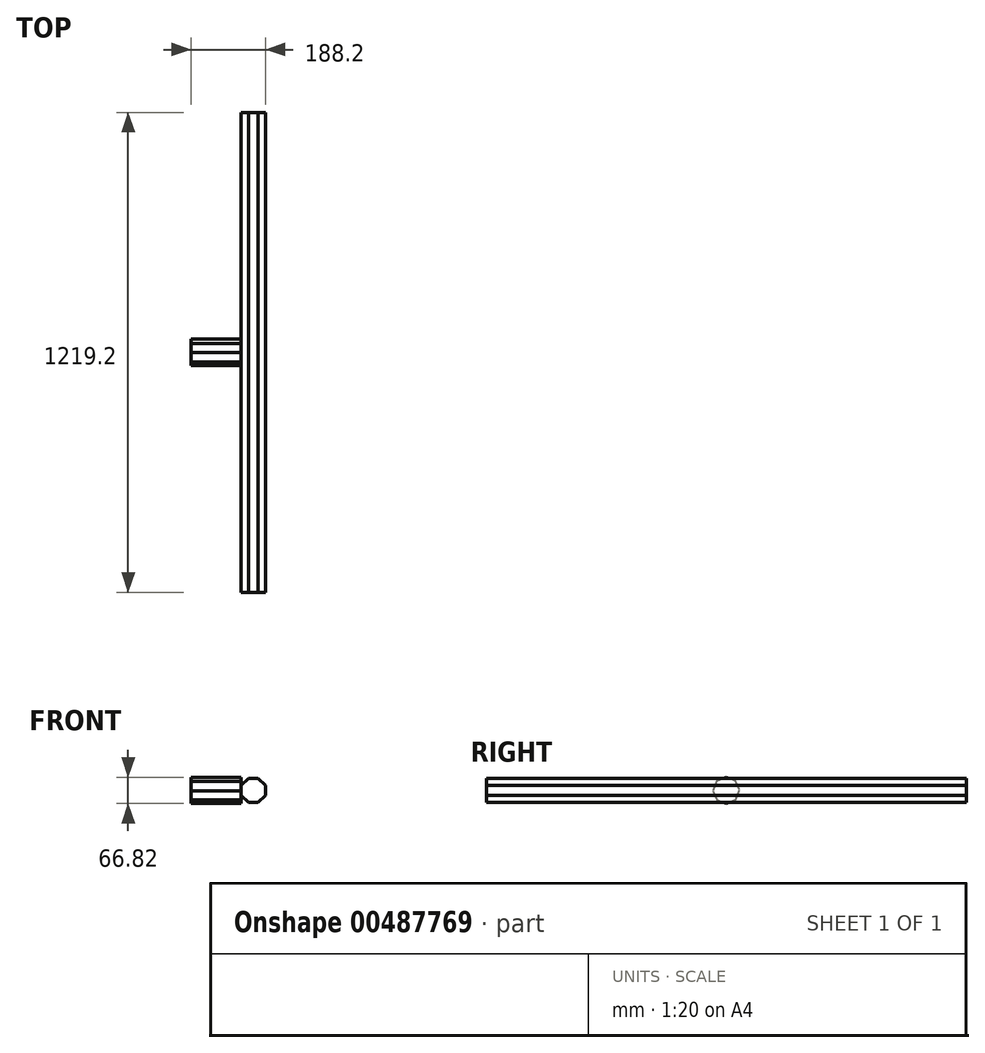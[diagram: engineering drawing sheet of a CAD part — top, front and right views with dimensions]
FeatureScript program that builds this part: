
annotation { "Feature Type Name" : "Feature", "Feature Type Description" : "" }
export const myFeature = defineFeature(function(context is Context, id is Id, definition is map)
    precondition{}
    {
        {
            var Q0;
            Q0=qCreatedBy(makeId("Front.planeOp"),FACE);
            var sketch = newSketch(context, id + "F0", { "sketchPlane" : qUnion([Q0])});
            skCircle(sketch, "E0.cCircle", {"center": v(0, 0) * mm, "radius": 30.6 * mm, "construction": true});
            skLineSegment(sketch, "E0.0", {"start": v(30.6, 12.68) * mm, "end": v(30.6, -12.68) * mm});
            skLineSegment(sketch, "E0.1", {"start": v(30.6, -12.68) * mm, "end": v(12.68, -30.6) * mm});
            skLineSegment(sketch, "E0.2", {"start": v(12.68, -30.6) * mm, "end": v(-12.68, -30.6) * mm});
            skLineSegment(sketch, "E0.3", {"start": v(-12.68, -30.6) * mm, "end": v(-30.6, -12.68) * mm});
            skLineSegment(sketch, "E0.4", {"start": v(-30.6, -12.68) * mm, "end": v(-30.6, 12.68) * mm});
            skLineSegment(sketch, "E0.5", {"start": v(-30.6, 12.68) * mm, "end": v(-12.68, 30.6) * mm});
            skLineSegment(sketch, "E0.6", {"start": v(-12.68, 30.6) * mm, "end": v(12.68, 30.6) * mm});
            skLineSegment(sketch, "E0.7", {"start": v(12.68, 30.6) * mm, "end": v(30.6, 12.68) * mm});
            skPoint(sketch, "E0.0.midPoint", {"position": v(30.6, 0) * mm});
            skSolve(sketch);
        }
        {
            var Q0;
            Q0=makeQuery(id+"F0.imprint","IMPRINT",FACE,{"disambiguationData":[TD([[makeQuery(id+"F0.imprint","IMPRINT",EDGE,{"derivedFrom":sQuery(id+"F0.wireOp",EDGE,"E0.0")}),-1.0]])]});
            extrude(context, id + "F1", {"entities" : qUnion([Q0]), "depth" : 1219.2 * mm});
        }
        {
            var Q0;
            Q0=makeQuery(id+"F1.opExtrude","SWEPT_FACE",FACE,{"disambiguationData":[OSD([sQuery(id+"F0.wireOp",EDGE,"E0.4")])]});
            var sketch = newSketch(context, id + "F2", { "sketchPlane" : qUnion([Q0])});
            skCircle(sketch, "E1.cCircle", {"center": v(609.6, 0) * mm, "radius": 30.88 * mm, "construction": true});
            skPoint(sketch, "E1.cCircle.centerSnap0", {"position": v(609.6, 12.68) * mm});
            skLineSegment(sketch, "E1.0", {"start": v(643, -1.02) * mm, "end": v(632.5, -24.34) * mm});
            skLineSegment(sketch, "E1.1", {"start": v(632.5, -24.34) * mm, "end": v(608.58, -33.4) * mm});
            skLineSegment(sketch, "E1.2", {"start": v(608.58, -33.4) * mm, "end": v(585.26, -22.9) * mm});
            skLineSegment(sketch, "E1.3", {"start": v(585.26, -22.9) * mm, "end": v(576.2, 1.02) * mm});
            skLineSegment(sketch, "E1.4", {"start": v(576.2, 1.02) * mm, "end": v(586.7, 24.34) * mm});
            skLineSegment(sketch, "E1.5", {"start": v(586.7, 24.34) * mm, "end": v(610.62, 33.4) * mm});
            skLineSegment(sketch, "E1.6", {"start": v(610.62, 33.4) * mm, "end": v(633.94, 22.9) * mm});
            skLineSegment(sketch, "E1.7", {"start": v(633.94, 22.9) * mm, "end": v(643, -1.02) * mm});
            skPoint(sketch, "E1.0.midPoint", {"position": v(637.75, -12.68) * mm});
            skSolve(sketch);
        }
        {
            var Q0;
            {var subQ4=sQuery(id+"F2.wireOp",EDGE,"E1.5");Q0=makeQuery(id+"F2.imprint","IMPRINT",FACE,{"disambiguationData":[TD([[makeQuery(id+"F2.imprint","IMPRINT",EDGE,{"derivedFrom":subQ4}),-1.0]])]});}
            var Q1;
            {var subQ0=sQuery(id+"F2.wireOp",EDGE,"E1.7");var subQ1=sQuery(id+"F2.wireOp",EDGE,"E1.0");var subQ2=makeQuery(id+"F2.imprint","INTERSECT",VERTEX,{"derivedFrom":[subQ1,subQ0]});Q1=makeQuery(id+"F2.imprint","IMPRINT",FACE,{"disambiguationData":[TD([[makeQuery(id+"F2.imprint","IMPRINT",EDGE,{"disambiguationData":[TD([[subQ2,-1.0]])],"derivedFrom":subQ1}),-1.0]])]});}
            var Q2;
            {var subQ4=sQuery(id+"F2.wireOp",EDGE,"E1.1");Q2=makeQuery(id+"F2.imprint","IMPRINT",FACE,{"disambiguationData":[TD([[makeQuery(id+"F2.imprint","IMPRINT",EDGE,{"derivedFrom":subQ4}),-1.0]])]});}
            extrude(context, id + "F3", {"entities" : qUnion([Q0, Q1, Q2]), "operationType" : NewBodyOperationType.ADD, "depth" : 127 * mm});
        }
    });
